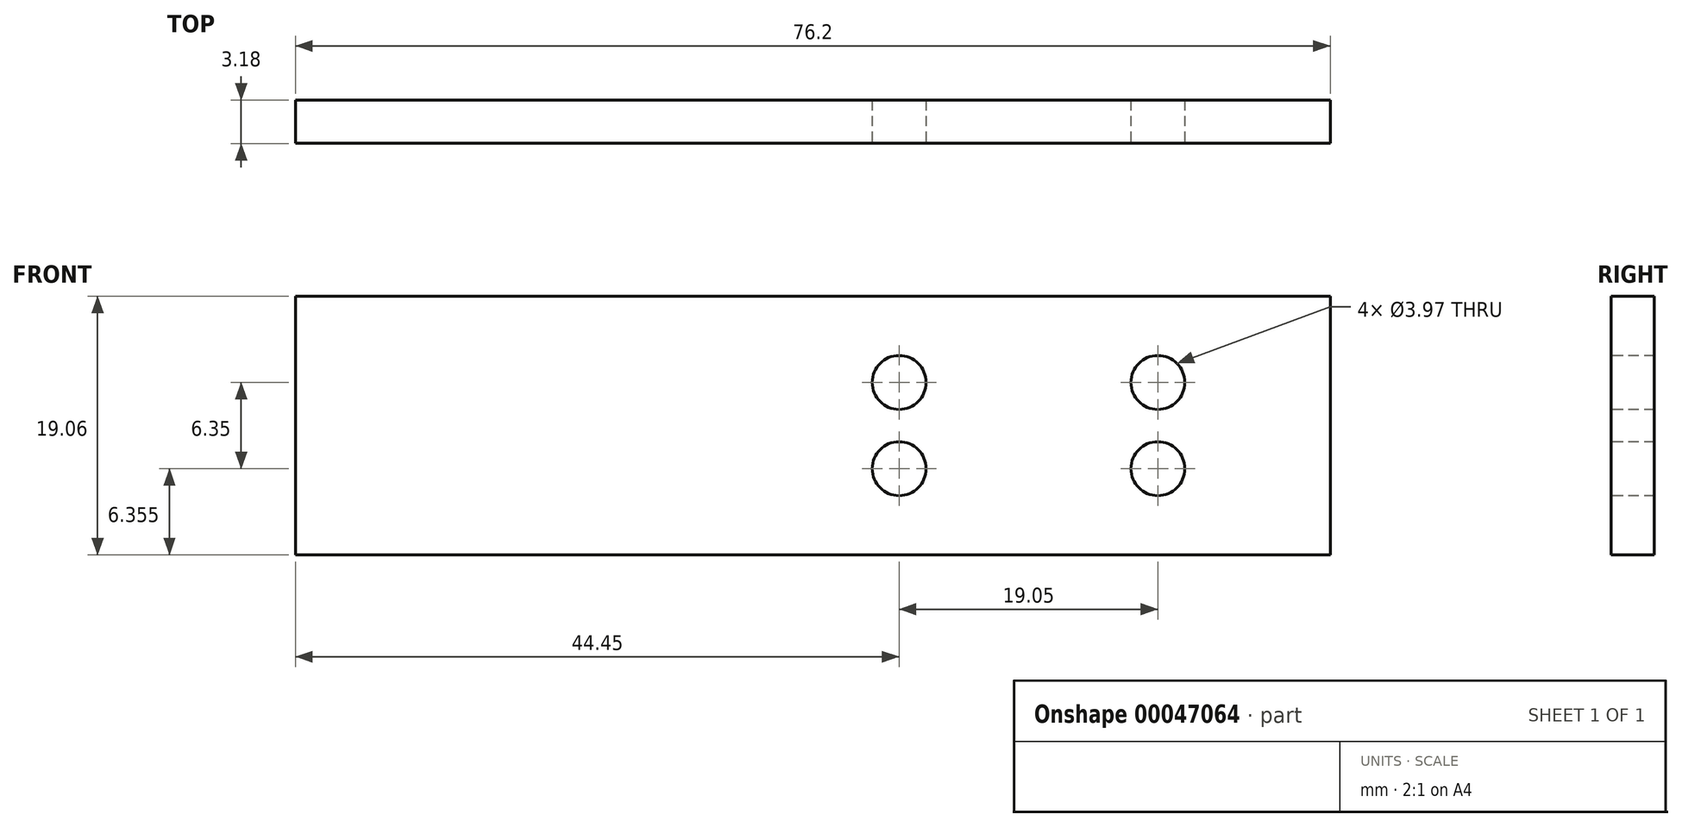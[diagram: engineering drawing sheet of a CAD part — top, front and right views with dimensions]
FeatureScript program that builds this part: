
annotation { "Feature Type Name" : "Feature", "Feature Type Description" : "" }
export const myFeature = defineFeature(function(context is Context, id is Id, definition is map)
    precondition{}
    {
        {
            var Q0;
            Q0=qCreatedBy(makeId("Right.planeOp"),FACE);
            var sketch = newSketch(context, id + "F0", { "sketchPlane" : qUnion([Q0])});
            skLineSegment(sketch, "E0.rect.bottom", {"start": v(1.59, -9.53) * mm, "end": v(-1.59, -9.53) * mm});
            skLineSegment(sketch, "E0.rect.top", {"start": v(1.59, 9.53) * mm, "end": v(-1.59, 9.53) * mm});
            skLineSegment(sketch, "E0.rect.left", {"start": v(1.59, -9.53) * mm, "end": v(1.59, 9.53) * mm});
            skLineSegment(sketch, "E0.rect.right", {"start": v(-1.59, -9.53) * mm, "end": v(-1.59, 9.53) * mm});
            skPoint(sketch, "E0.rect.middle", {"position": v(0, 0) * mm});
            skSolve(sketch);
        }
        {
            var Q0;
            Q0 = qSketchRegion(id + "F0", true);
            extrude(context, id + "F1", {"entities" : qUnion([Q0]), "endBound" : BoundingType.SYMMETRIC, "depth" : 76.2 * mm});
        }
        {
            var Q0;
            Q0=makeQuery(id+"F1.opExtrude","SWEPT_FACE",FACE,{"disambiguationData":[OSD([sQuery(id+"F0.wireOp",EDGE,"E0.rect.right")])]});
            var sketch = newSketch(context, id + "F2", { "sketchPlane" : qUnion([Q0])});
            skCircle(sketch, "E1", {"center": v(25.4, -3.17) * mm, "radius": 1.98 * mm});
            skCircle(sketch, "E2", {"center": v(6.35, -3.17) * mm, "radius": 1.98 * mm});
            skCircle(sketch, "E3.MirrorC", {"center": v(25.4, 3.17) * mm, "radius": 1.98 * mm});
            skCircle(sketch, "E4.MirrorC", {"center": v(6.35, 3.17) * mm, "radius": 1.98 * mm});
            skSolve(sketch);
        }
        {
            var Q0;
            Q0 = qSketchRegion(id + "F2", true);
            var Q1;
            Q1=makeQuery(id+"F1.opExtrude","SWEPT_FACE",FACE,{"disambiguationData":[OSD([sQuery(id+"F0.wireOp",EDGE,"E0.rect.left")])]});
            extrude(context, id + "F3", {"entities" : qUnion([Q0]), "operationType" : NewBodyOperationType.REMOVE, "endBound" : BoundingType.UP_TO_SURFACE, "oppositeDirection" : true, "endBoundEntityFace" : qUnion([Q1]), "depth" : 25.4 * mm});
        }
    });
